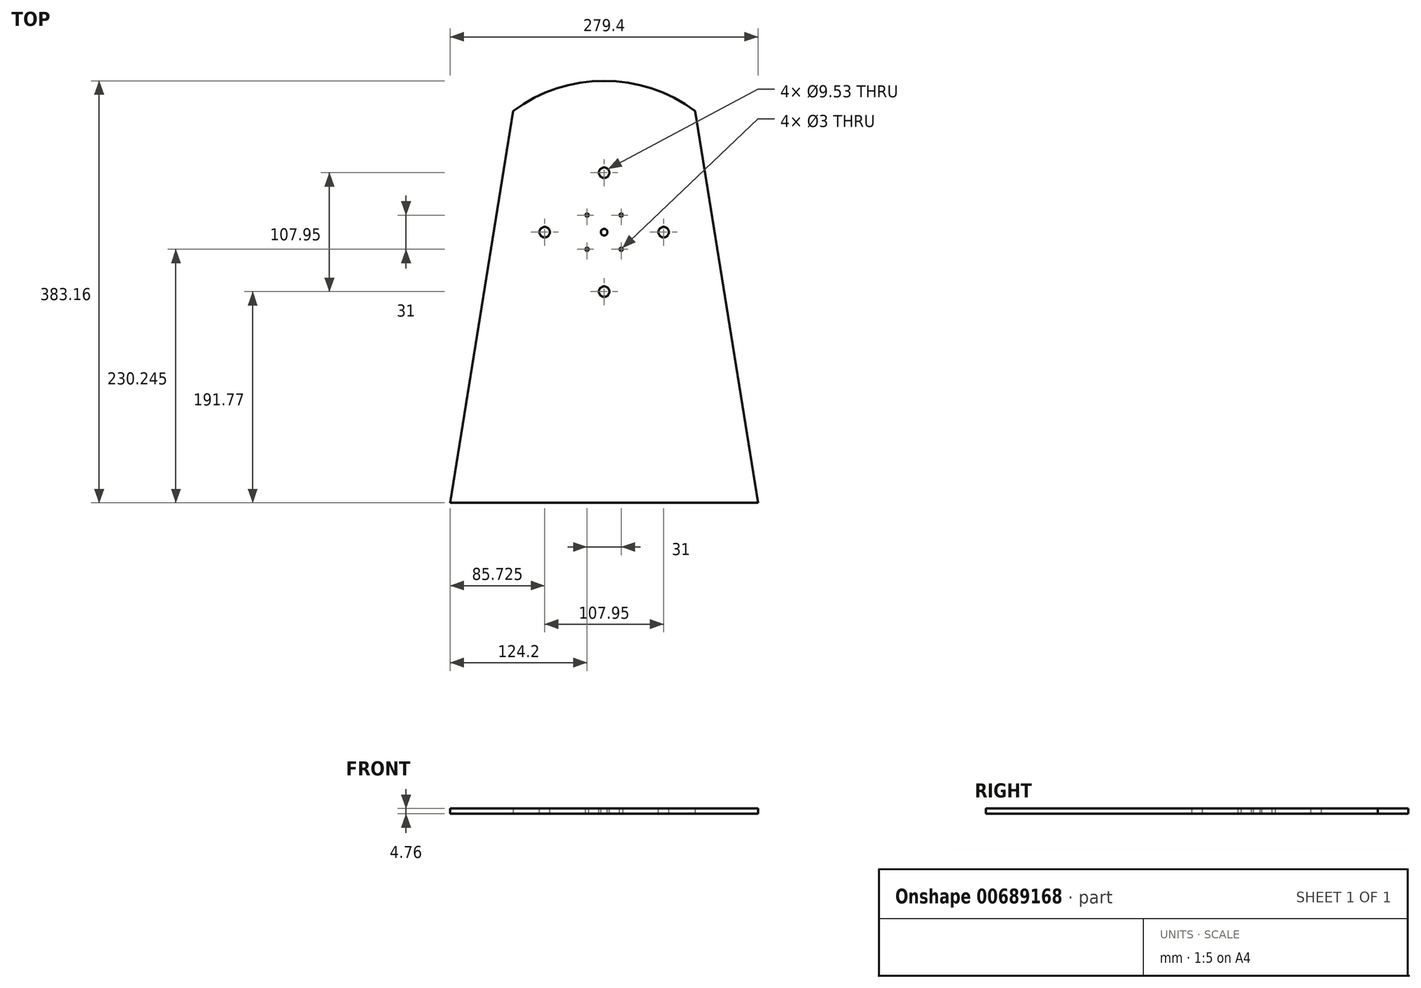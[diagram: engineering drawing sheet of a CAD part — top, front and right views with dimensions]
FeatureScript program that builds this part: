
annotation { "Feature Type Name" : "Feature", "Feature Type Description" : "" }
export const myFeature = defineFeature(function(context is Context, id is Id, definition is map)
    precondition{}
    {
        {
            var Q0;
            Q0=qCreatedBy(makeId("Top.planeOp"),FACE);
            var sketch = newSketch(context, id + "F0", { "sketchPlane" : qUnion([Q0])});
            skLineSegment(sketch, "E0.bottom", {"start": v(82.55, -177.8) * mm, "end": v(-82.55, -177.8) * mm});
            skLineSegment(sketch, "E0.top", {"start": v(82.55, 177.8) * mm, "end": v(-82.55, 177.8) * mm});
            skLineSegment(sketch, "E0.left", {"start": v(82.55, -177.8) * mm, "end": v(82.55, 177.8) * mm});
            skLineSegment(sketch, "E0.right", {"start": v(-82.55, -177.8) * mm, "end": v(-82.55, 177.8) * mm});
            skPoint(sketch, "E0.middle", {"position": v(0, 0) * mm});
            skLineSegment(sketch, "E1", {"start": v(-82.55, 177.8) * mm, "end": v(-139.7, -177.8) * mm});
            skLineSegment(sketch, "E2", {"start": v(-139.7, -177.8) * mm, "end": v(-82.55, -177.8) * mm});
            skLineSegment(sketch, "E3", {"start": v(0, 177.8) * mm, "end": v(0, -177.8) * mm});
            skLineSegment(sketch, "E4.MirrorCS", {"start": v(82.55, 177.8) * mm, "end": v(139.7, -177.8) * mm});
            skLineSegment(sketch, "E5.MirrorCS", {"start": v(139.7, -177.8) * mm, "end": v(82.55, -177.8) * mm});
            skSolve(sketch);
        }
        {
            var Q0;
            Q0=qSketchRegion(id+"F0",true);
            extrude(context, id + "F1", {"entities" : qUnion([Q0]), "depth" : 4.76 * mm});
        }
        {
            var Q0;
            Q0=makeQuery(id+"F1.opExtrude","CAP_FACE",FACE,{"disambiguationData":[OSD([sQuery(id+"F0.wireOp",EDGE,"E0.bottom"),sQuery(id+"F0.wireOp",EDGE,"E0.top"),sQuery(id+"F0.wireOp",EDGE,"E1"),sQuery(id+"F0.wireOp",EDGE,"E2"),sQuery(id+"F0.wireOp",EDGE,"E4.MirrorCS"),sQuery(id+"F0.wireOp",EDGE,"E5.MirrorCS")])],"isStart":false});
            var sketch = newSketch(context, id + "F2", { "sketchPlane" : qUnion([Q0])});
            skPoint(sketch, "E6", {"position": v(0, 67.95) * mm});
            skPoint(sketch, "E6.positionSnap0", {"position": v(0, 177.8) * mm});
            skPoint(sketch, "E7", {"position": v(0, 121.92) * mm});
            skPoint(sketch, "E8", {"position": v(53.98, 67.95) * mm});
            skPoint(sketch, "E9", {"position": v(0, 13.97) * mm});
            skPoint(sketch, "E10", {"position": v(-53.98, 67.95) * mm});
            skPoint(sketch, "E11", {"position": v(-15.5, 83.45) * mm});
            skPoint(sketch, "E12.0.1.0", {"position": v(-15.5, 52.45) * mm});
            skPoint(sketch, "E12.1.0.0", {"position": v(15.5, 83.45) * mm});
            skPoint(sketch, "E12.1.1.0", {"position": v(15.5, 52.45) * mm});
            skLineSegment(sketch, "E12.direction1", {"start": v(-15.5, 83.45) * mm, "end": v(15.5, 83.45) * mm, "construction": true});
            skLineSegment(sketch, "E12.direction2", {"start": v(-15.5, 83.45) * mm, "end": v(-15.5, 52.45) * mm, "construction": true});
            skSolve(sketch);
        }
        {
            var Q0;
            Q0=sQuery(id+"F2.wireOp",VERTEX,"E10");
            var Q1;
            Q1=sQuery(id+"F2.wireOp",VERTEX,"E7");
            var Q2;
            Q2=sQuery(id+"F2.wireOp",VERTEX,"E8");
            var Q3;
            Q3=sQuery(id+"F2.wireOp",VERTEX,"E9");
            var Q4;
            Q4=makeQuery(id+"F1.opExtrude","SWEPT_BODY",BODY,{"disambiguationData":[OSD([sQuery(id+"F0.wireOp",EDGE,"E0.bottom"),sQuery(id+"F0.wireOp",EDGE,"E0.top"),sQuery(id+"F0.wireOp",EDGE,"E1"),sQuery(id+"F0.wireOp",EDGE,"E2"),sQuery(id+"F0.wireOp",EDGE,"E4.MirrorCS"),sQuery(id+"F0.wireOp",EDGE,"E5.MirrorCS")])]});
            hole(context, id + "F3", {"style" : HoleStyle.SIMPLE, "endStyle" : HoleEndStyle.THROUGH, "holeDiameter" : 9.52 * mm, "isTappedThrough" : true, "tappedDepth" : 12.7 * mm, "tapClearance" : 3, "locations" : qUnion([Q0, Q1, Q2, Q3]), "scope" : qUnion([Q4])});
        }
        {
            var Q0;
            Q0=sQuery(id+"F2.wireOp",VERTEX,"E12.1.0.0");
            var Q1;
            Q1=sQuery(id+"F2.wireOp",VERTEX,"E11");
            var Q2;
            Q2=sQuery(id+"F2.wireOp",VERTEX,"E12.0.1.0");
            var Q3;
            Q3=sQuery(id+"F2.wireOp",VERTEX,"E12.1.1.0");
            var Q4;
            Q4=makeQuery(id+"F1.opExtrude","SWEPT_BODY",BODY,{"disambiguationData":[OSD([sQuery(id+"F0.wireOp",EDGE,"E0.bottom"),sQuery(id+"F0.wireOp",EDGE,"E0.top"),sQuery(id+"F0.wireOp",EDGE,"E1"),sQuery(id+"F0.wireOp",EDGE,"E2"),sQuery(id+"F0.wireOp",EDGE,"E4.MirrorCS"),sQuery(id+"F0.wireOp",EDGE,"E5.MirrorCS")])]});
            hole(context, id + "F4", {"style" : HoleStyle.SIMPLE, "endStyle" : HoleEndStyle.THROUGH, "holeDiameter" : 3 * mm, "isTappedThrough" : true, "tappedDepth" : 12.7 * mm, "tapClearance" : 3, "locations" : qUnion([Q0, Q1, Q2, Q3]), "scope" : qUnion([Q4])});
        }
        {
            var Q0;
            Q0=sQuery(id+"F2.wireOp",VERTEX,"E6");
            var Q1;
            Q1=makeQuery(id+"F1.opExtrude","SWEPT_BODY",BODY,{"disambiguationData":[OSD([sQuery(id+"F0.wireOp",EDGE,"E0.bottom"),sQuery(id+"F0.wireOp",EDGE,"E0.top"),sQuery(id+"F0.wireOp",EDGE,"E1"),sQuery(id+"F0.wireOp",EDGE,"E2"),sQuery(id+"F0.wireOp",EDGE,"E4.MirrorCS"),sQuery(id+"F0.wireOp",EDGE,"E5.MirrorCS")])]});
            hole(context, id + "F5", {"style" : HoleStyle.SIMPLE, "endStyle" : HoleEndStyle.THROUGH, "holeDiameter" : 6 * mm, "isTappedThrough" : true, "tappedDepth" : 12.7 * mm, "tapClearance" : 3, "locations" : qUnion([Q0]), "scope" : qUnion([Q1])});
        }
        {
            var Q0;
            Q0=makeQuery(id+"F2.imprint","IMPRINT",FACE,{"disambiguationData":[TD([[makeQuery(id+"F2.imprint","IMPRINT",EDGE,{"derivedFrom":makeQuery(id+"F1.opExtrude","CAP_EDGE",EDGE,{"disambiguationData":[OSD([sQuery(id+"F0.wireOp",EDGE,"E0.top")])],"isStart":false})}),1.0]])]});
            var sketch = newSketch(context, id + "F6", { "sketchPlane" : qUnion([Q0])});
            skPoint(sketch, "E13.0", {"position": v(0, 67.95) * mm});
            skPoint(sketch, "E14.0", {"position": v(82.55, 177.8) * mm});
            skArc(sketch, "E15", {"start": v(82.55, 177.8) * mm, "mid": v(0, 205.36) * mm, "end": v(-82.55, 177.8) * mm});
            skPoint(sketch, "E16.0", {"position": v(-82.55, 177.8) * mm});
            skSolve(sketch);
        }
        {
            var Q0;
            Q0=makeQuery(id+"F6.imprint","IMPRINT",FACE,{"disambiguationData":[TD([[makeQuery(id+"F6.imprint","IMPRINT",EDGE,{"derivedFrom":sQuery(id+"F6.wireOp",EDGE,"E15")}),1.0]])]});
            extrude(context, id + "F7", {"entities" : qUnion([Q0]), "operationType" : NewBodyOperationType.ADD, "oppositeDirection" : true, "depth" : 4.76 * mm, "offsetDistance" : 25.4 * mm});
        }
    });
